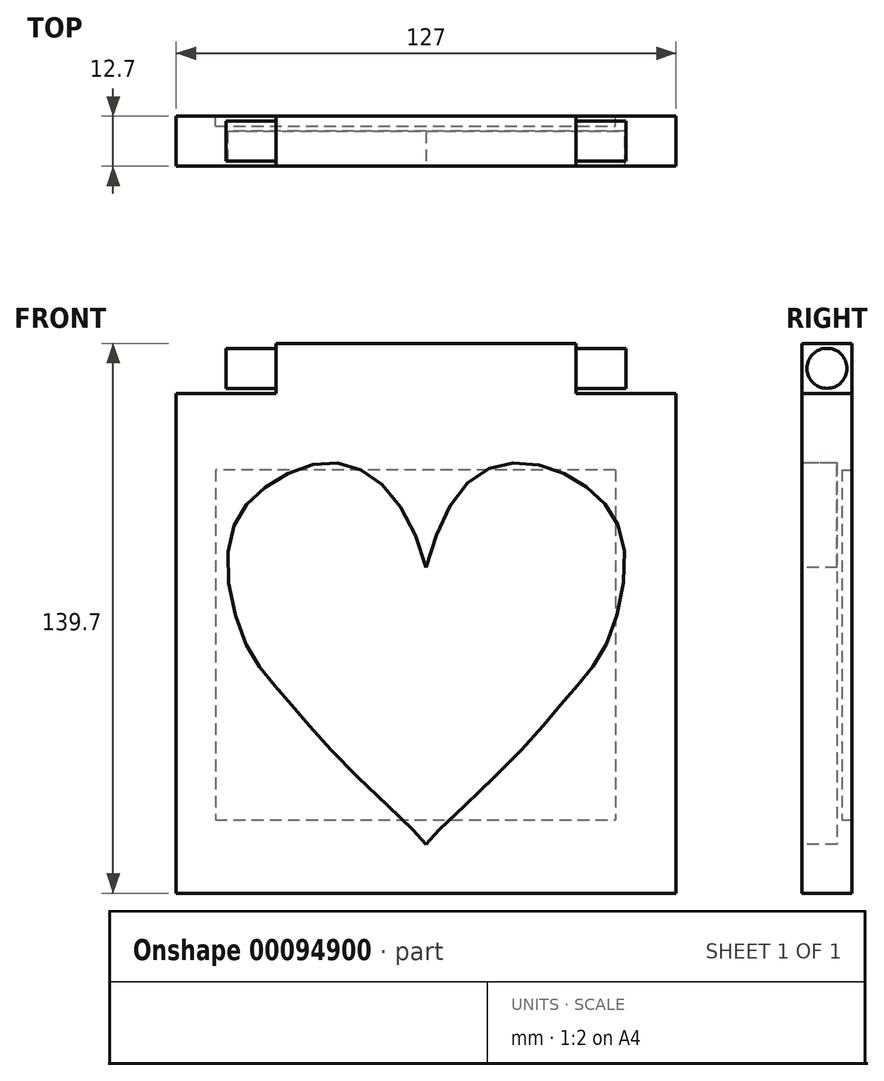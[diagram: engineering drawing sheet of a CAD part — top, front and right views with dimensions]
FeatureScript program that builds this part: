
annotation { "Feature Type Name" : "Feature", "Feature Type Description" : "" }
export const myFeature = defineFeature(function(context is Context, id is Id, definition is map)
    precondition{}
    {
        {
            var Q0;
            Q0=qCreatedBy(makeId("Front.planeOp"),FACE);
            var sketch = newSketch(context, id + "F0", { "sketchPlane" : qUnion([Q0])});
            skLineSegment(sketch, "E0", {"start": v(0, 0) * mm, "end": v(0, 127) * mm});
            skLineSegment(sketch, "E1", {"start": v(0, 127) * mm, "end": v(127, 127) * mm});
            skLineSegment(sketch, "E2", {"start": v(127, 127) * mm, "end": v(127, 0) * mm});
            skLineSegment(sketch, "E3", {"start": v(127, 0) * mm, "end": v(0, 0) * mm});
            skLineSegment(sketch, "E4", {"start": v(25.4, 127) * mm, "end": v(25.4, 139.7) * mm});
            skLineSegment(sketch, "E5", {"start": v(25.4, 139.7) * mm, "end": v(101.6, 139.7) * mm});
            skLineSegment(sketch, "E6", {"start": v(101.6, 139.7) * mm, "end": v(101.6, 127) * mm});
            skSolve(sketch);
        }
        {
            var Q0;
            Q0=qSketchRegion(id+"F0",true);
            extrude(context, id + "F1", {"entities" : qUnion([Q0]), "depth" : 12.7 * mm});
        }
        {
            var Q0;
            Q0=makeQuery(id+"F1.opExtrude","CAP_FACE",FACE,{"disambiguationData":[OSD([sQuery(id+"F0.wireOp",EDGE,"E0"),sQuery(id+"F0.wireOp",EDGE,"E1"),sQuery(id+"F0.wireOp",EDGE,"E2"),sQuery(id+"F0.wireOp",EDGE,"E3")])],"isStart":false});
            var sketch = newSketch(context, id + "F2", { "sketchPlane" : qUnion([Q0])});
            skFitSpline(sketch, "E7", {"points": [v(63.5, 82.82) * mm, v(74.7, 104.87) * mm, v(89.84, 109.22) * mm, v(105.74, 102.05) * mm, v(113.69, 88.31) * mm, v(109.35, 63.5) * mm, v(99.7, 50.22) * mm, v(83.33, 31.94) * mm, v(63.5, 12.43) * mm, v(63.5, 11.7) * mm], "startDerivative": vector(51.6, 197.91) * mm, "endDerivative": vector(16.47, -31.24) * mm});
            skFitSpline(sketch, "E8.MirrorCS", {"points": [v(63.5, 82.82) * mm, v(51.57, 104.5) * mm, v(37.16, 109.27) * mm, v(21.26, 102.05) * mm, v(13.31, 88.31) * mm, v(17.65, 63.5) * mm, v(27.3, 50.22) * mm, v(43.67, 31.94) * mm, v(63.5, 12.43) * mm, v(63.5, 11.7) * mm], "startDerivative": vector(-51.6, 197.91) * mm, "endDerivative": vector(-16.47, -31.24) * mm});
            skSolve(sketch);
        }
        {
            var Q0;
            Q0=qSketchRegion(id+"F2",true);
            extrude(context, id + "F3", {"entities" : qUnion([Q0]), "operationType" : NewBodyOperationType.REMOVE, "oppositeDirection" : true, "depth" : 8.9 * mm});
        }
        {
            var Q0;
            Q0=makeQuery(id+"F1.opExtrude","SWEPT_FACE",FACE,{"disambiguationData":[OSD([sQuery(id+"F0.wireOp",EDGE,"E4")])]});
            var sketch = newSketch(context, id + "F4", { "sketchPlane" : qUnion([Q0])});
            skCircle(sketch, "E9", {"center": v(6.35, 133.35) * mm, "radius": 5.08 * mm});
            skSolve(sketch);
        }
        {
            var Q0;
            Q0=makeQuery(id+"F1.opExtrude","SWEPT_FACE",FACE,{"disambiguationData":[OSD([sQuery(id+"F0.wireOp",EDGE,"E6")])]});
            var sketch = newSketch(context, id + "F5", { "sketchPlane" : qUnion([Q0])});
            skCircle(sketch, "E10", {"center": v(-6.35, 133.35) * mm, "radius": 5.08 * mm});
            skSolve(sketch);
        }
        {
            var Q0;
            Q0=makeQuery(id+"F4.imprint","IMPRINT",FACE,{"disambiguationData":[TD([[makeQuery(id+"F4.imprint","IMPRINT",EDGE,{"derivedFrom":sQuery(id+"F4.wireOp",EDGE,"E9")}),1.0]])]});
            extrude(context, id + "F6", {"entities" : qUnion([Q0]), "operationType" : NewBodyOperationType.ADD, "depth" : 12.7 * mm});
        }
        {
            var Q0;
            Q0=makeQuery(id+"F5.imprint","IMPRINT",FACE,{"disambiguationData":[TD([[makeQuery(id+"F5.imprint","IMPRINT",EDGE,{"derivedFrom":sQuery(id+"F5.wireOp",EDGE,"E10")}),1.0]])]});
            extrude(context, id + "F7", {"entities" : qUnion([Q0]), "operationType" : NewBodyOperationType.ADD, "depth" : 12.7 * mm});
        }
        {
            var Q0;
            Q0=makeQuery(id+"F1.opExtrude","CAP_FACE",FACE,{"disambiguationData":[OSD([sQuery(id+"F0.wireOp",EDGE,"E0"),sQuery(id+"F0.wireOp",EDGE,"E1"),sQuery(id+"F0.wireOp",EDGE,"E2"),sQuery(id+"F0.wireOp",EDGE,"E3"),sQuery(id+"F0.wireOp",EDGE,"E4"),sQuery(id+"F0.wireOp",EDGE,"E5"),sQuery(id+"F0.wireOp",EDGE,"E6")])],"isStart":true});
            var sketch = newSketch(context, id + "F8", { "sketchPlane" : qUnion([Q0])});
            skLineSegment(sketch, "E11.top", {"start": v(-63.5, 18.67) * mm, "end": v(-111.58, 18.67) * mm});
            skLineSegment(sketch, "E11.right", {"start": v(-111.58, 63.5) * mm, "end": v(-111.58, 18.67) * mm});
            skLineSegment(sketch, "E12.top", {"start": v(-63.5, 107.57) * mm, "end": v(-111.58, 107.57) * mm});
            skLineSegment(sketch, "E12.right", {"start": v(-111.58, 50.8) * mm, "end": v(-111.58, 107.57) * mm});
            skLineSegment(sketch, "E13.top", {"start": v(-63.5, 107.57) * mm, "end": v(-9.98, 107.57) * mm});
            skLineSegment(sketch, "E13.right", {"start": v(-9.98, 50.8) * mm, "end": v(-9.98, 107.57) * mm});
            skLineSegment(sketch, "E14.top", {"start": v(-63.5, 18.67) * mm, "end": v(-9.98, 18.67) * mm});
            skLineSegment(sketch, "E14.right", {"start": v(-9.98, 63.5) * mm, "end": v(-9.98, 18.67) * mm});
            skSolve(sketch);
        }
        {
            var Q0;
            Q0 = qSketchRegion(id + "F8", true);
            extrude(context, id + "F9", {"entities" : qUnion([Q0]), "operationType" : NewBodyOperationType.ADD, "depth" : 25.4 * mm});
        }
        {
            var Q0;
            Q0=makeQuery(id+"F9.opExtrude","CAP_FACE",FACE,{"disambiguationData":[OSD([sQuery(id+"F8.wireOp",EDGE,"E11.top"),sQuery(id+"F8.wireOp",EDGE,"E11.right"),sQuery(id+"F8.wireOp",EDGE,"E12.top"),sQuery(id+"F8.wireOp",EDGE,"E12.right"),sQuery(id+"F8.wireOp",EDGE,"E13.top"),sQuery(id+"F8.wireOp",EDGE,"E13.right"),sQuery(id+"F8.wireOp",EDGE,"E14.top"),sQuery(id+"F8.wireOp",EDGE,"E14.right")])],"isStart":false});
            extrude(context, id + "F10", {"entities" : qUnion([Q0]), "operationType" : NewBodyOperationType.REMOVE, "oppositeDirection" : true, "depth" : 27.94 * mm});
        }
    });
